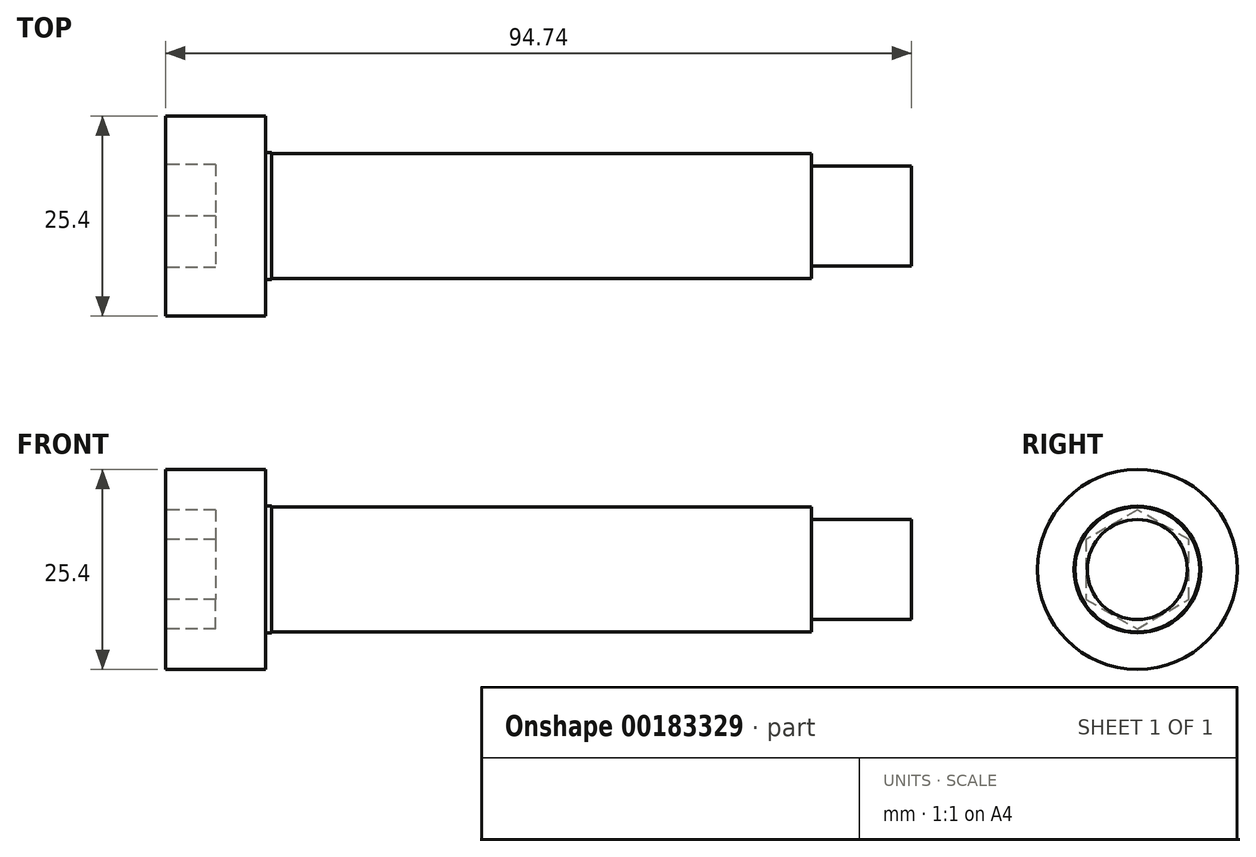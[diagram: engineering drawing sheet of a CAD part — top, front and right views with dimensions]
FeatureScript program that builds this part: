
annotation { "Feature Type Name" : "Feature", "Feature Type Description" : "" }
export const myFeature = defineFeature(function(context is Context, id is Id, definition is map)
    precondition{}
    {
        {
            var Q0;
            Q0=qCreatedBy(makeId("Right.planeOp"),FACE);
            var sketch = newSketch(context, id + "F0", { "sketchPlane" : qUnion([Q0])});
            skCircle(sketch, "E0", {"center": v(0, 0) * mm, "radius": 12.7 * mm});
            skSolve(sketch);
        }
        {
            var Q0;
            Q0 = qSketchRegion(id + "F0", true);
            extrude(context, id + "F1", {"entities" : qUnion([Q0]), "endBound" : BoundingType.SYMMETRIC, "depth" : 12.7 * mm});
        }
        {
            var Q0;
            Q0=makeQuery(id+"F1.opExtrude","CAP_FACE",FACE,{"disambiguationData":[OSD([sQuery(id+"F0.wireOp",EDGE,"E0")])],"isStart":false});
            var sketch = newSketch(context, id + "F2", { "sketchPlane" : qUnion([Q0])});
            skCircle(sketch, "E1", {"center": v(0, 0) * mm, "radius": 8.06 * mm});
            skSolve(sketch);
        }
        {
            var Q0;
            Q0 = qSketchRegion(id + "F2", true);
            extrude(context, id + "F3", {"entities" : qUnion([Q0]), "operationType" : NewBodyOperationType.ADD, "depth" : 0.76 * mm});
        }
        {
            var Q0;
            Q0=makeQuery(id+"F3.opExtrude","CAP_FACE",FACE,{"disambiguationData":[OSD([sQuery(id+"F2.wireOp",EDGE,"E1")])],"isStart":false});
            var sketch = newSketch(context, id + "F4", { "sketchPlane" : qUnion([Q0])});
            skCircle(sketch, "E2", {"center": v(0, 0) * mm, "radius": 7.94 * mm});
            skSolve(sketch);
        }
        {
            var Q0;
            Q0 = qSketchRegion(id + "F4", true);
            extrude(context, id + "F5", {"entities" : qUnion([Q0]), "operationType" : NewBodyOperationType.ADD, "depth" : 68.58 * mm});
        }
        {
            var Q0;
            Q0=makeQuery(id+"F5.opExtrude","CAP_FACE",FACE,{"disambiguationData":[OSD([sQuery(id+"F4.wireOp",EDGE,"E2")])],"isStart":false});
            var sketch = newSketch(context, id + "F6", { "sketchPlane" : qUnion([Q0])});
            skCircle(sketch, "E3", {"center": v(0, 0) * mm, "radius": 6.35 * mm});
            skSolve(sketch);
        }
        {
            var Q0;
            Q0 = qSketchRegion(id + "F6", true);
            extrude(context, id + "F7", {"entities" : qUnion([Q0]), "operationType" : NewBodyOperationType.ADD, "depth" : 12.7 * mm});
        }
        {
            var Q0;
            Q0=makeQuery(id+"F1.opExtrude","CAP_FACE",FACE,{"disambiguationData":[OSD([sQuery(id+"F0.wireOp",EDGE,"E0")])],"isStart":true});
            var sketch = newSketch(context, id + "F8", { "sketchPlane" : qUnion([Q0])});
            skCircle(sketch, "E4.cCircle", {"center": v(0, 0) * mm, "radius": 6.56 * mm, "construction": true});
            skLineSegment(sketch, "E4.0", {"start": v(6.56, 3.78) * mm, "end": v(6.56, -3.78) * mm});
            skLineSegment(sketch, "E4.1", {"start": v(6.56, -3.78) * mm, "end": v(0, -7.57) * mm});
            skLineSegment(sketch, "E4.2", {"start": v(0, -7.57) * mm, "end": v(-6.56, -3.78) * mm});
            skLineSegment(sketch, "E4.3", {"start": v(-6.56, -3.78) * mm, "end": v(-6.56, 3.78) * mm});
            skLineSegment(sketch, "E4.4", {"start": v(-6.56, 3.78) * mm, "end": v(0, 7.57) * mm});
            skLineSegment(sketch, "E4.5", {"start": v(0, 7.57) * mm, "end": v(6.56, 3.78) * mm});
            skPoint(sketch, "E4.0.midPoint", {"position": v(6.56, 0) * mm});
            skSolve(sketch);
        }
        {
            var Q0;
            Q0 = qSketchRegion(id + "F8", true);
            extrude(context, id + "F9", {"entities" : qUnion([Q0]), "operationType" : NewBodyOperationType.REMOVE, "oppositeDirection" : true, "depth" : 6.35 * mm});
        }
    });
